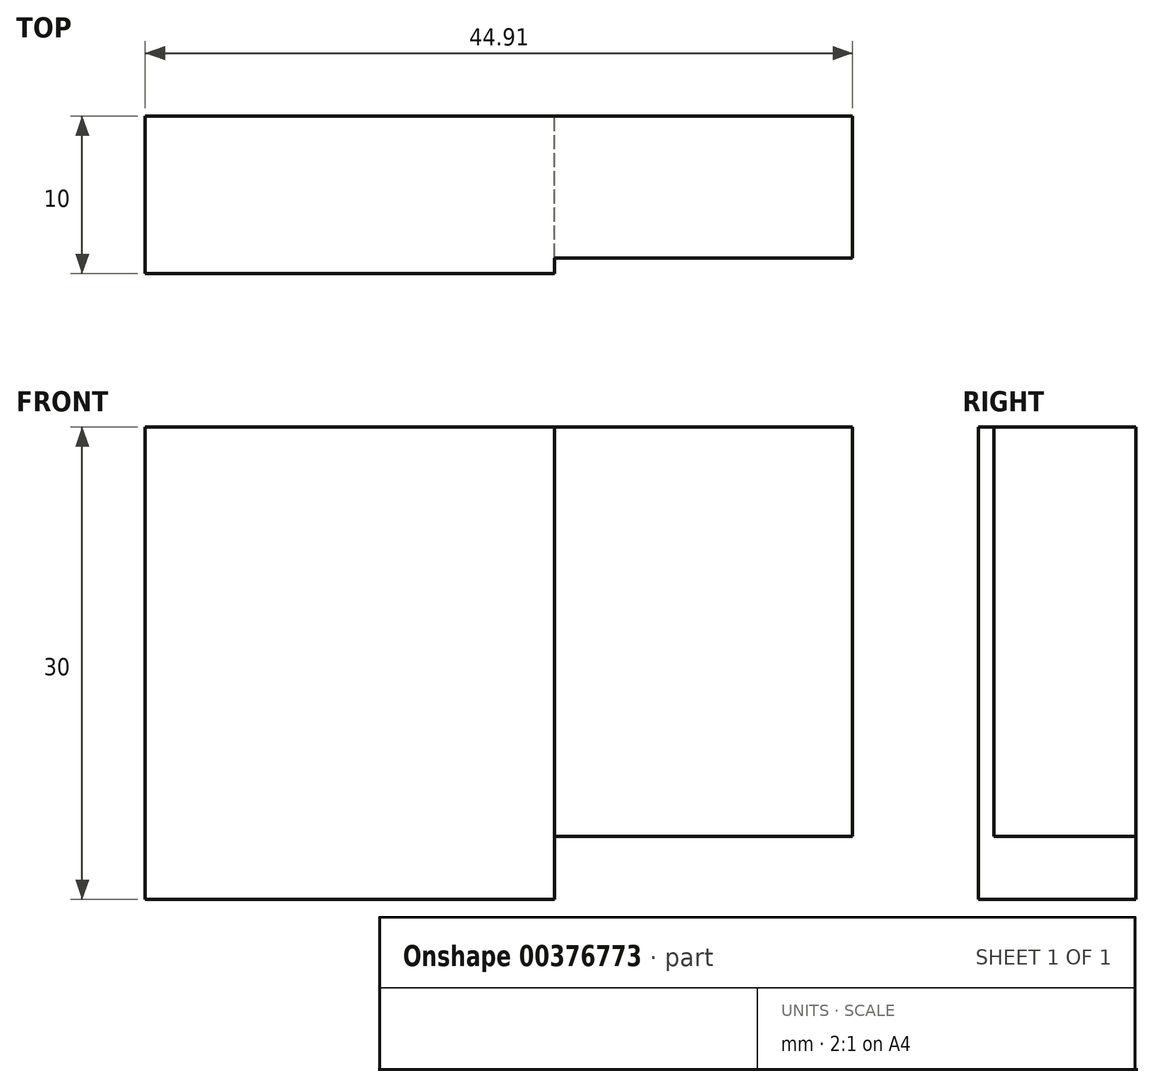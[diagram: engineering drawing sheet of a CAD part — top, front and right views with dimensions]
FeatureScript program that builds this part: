
annotation { "Feature Type Name" : "Feature", "Feature Type Description" : "" }
export const myFeature = defineFeature(function(context is Context, id is Id, definition is map)
    precondition{}
    {
        {
            var Q0;
            Q0=qCreatedBy(makeId("Front.planeOp"),FACE);
            var sketch = newSketch(context, id + "F0", { "sketchPlane" : qUnion([Q0])});
            skLineSegment(sketch, "E0.bottom", {"start": v(0, 0) * mm, "end": v(-26, 0) * mm});
            skLineSegment(sketch, "E0.top", {"start": v(0, -30) * mm, "end": v(-26, -30) * mm});
            skLineSegment(sketch, "E0.left", {"start": v(0, 0) * mm, "end": v(0, -30) * mm});
            skLineSegment(sketch, "E0.right", {"start": v(-26, 0) * mm, "end": v(-26, -30) * mm});
            skLineSegment(sketch, "E1.bottom", {"start": v(0, 0) * mm, "end": v(18.9, 0) * mm});
            skLineSegment(sketch, "E1.top", {"start": v(0, -26) * mm, "end": v(18.9, -26) * mm});
            skLineSegment(sketch, "E1.left", {"start": v(0, 0) * mm, "end": v(0, -26) * mm});
            skLineSegment(sketch, "E1.right", {"start": v(18.9, 0) * mm, "end": v(18.9, -26) * mm});
            skSolve(sketch);
        }
        {
            var Q0;
            Q0=makeQuery(id+"F0.imprint","IMPRINT",FACE,{"disambiguationData":[TD([[makeQuery(id+"F0.imprint","IMPRINT",EDGE,{"derivedFrom":sQuery(id+"F0.wireOp",EDGE,"E0.bottom")}),1.0]])]});
            extrude(context, id + "F1", {"entities" : qUnion([Q0]), "depth" : 10 * mm});
        }
        {
            var Q0;
            Q0=makeQuery(id+"F0.imprint","IMPRINT",FACE,{"disambiguationData":[TD([[makeQuery(id+"F0.imprint","IMPRINT",EDGE,{"derivedFrom":sQuery(id+"F0.wireOp",EDGE,"E1.bottom")}),-1.0]])]});
            extrude(context, id + "F2", {"entities" : qUnion([Q0]), "operationType" : NewBodyOperationType.ADD, "depth" : 9 * mm});
        }
        {
            var Q0;
            Q0=makeQuery(id+"F0.imprint","IMPRINT",FACE,{"disambiguationData":[TD([[makeQuery(id+"F0.imprint","IMPRINT",EDGE,{"derivedFrom":sQuery(id+"F0.wireOp",EDGE,"E1.bottom")}),-1.0]])]});
            var sketch = newSketch(context, id + "F3", { "sketchPlane" : qUnion([Q0])});
            skLineSegment(sketch, "E2.bottom", {"start": v(0, 0) * mm, "end": v(21.38, 0) * mm});
            skLineSegment(sketch, "E2.top", {"start": v(0, -30.42) * mm, "end": v(21.38, -30.42) * mm});
            skLineSegment(sketch, "E2.left", {"start": v(0, 0) * mm, "end": v(0, -30.42) * mm});
            skLineSegment(sketch, "E2.right", {"start": v(21.38, 0) * mm, "end": v(21.38, -30.42) * mm});
            skSolve(sketch);
        }
        {
            var Q0;
            {var subQ3=sQuery(id+"F3.wireOp",EDGE,"E2.top");Q0=makeQuery(id+"F3.imprint","IMPRINT",FACE,{"disambiguationData":[TD([[makeQuery(id+"F3.imprint","IMPRINT",EDGE,{"derivedFrom":subQ3}),1.0]])]});}
            extrude(context, id + "F4", {"entities" : qUnion([Q0]), "operationType" : NewBodyOperationType.REMOVE, "oppositeDirection" : true, "depth" : -1 * mm});
        }
    });
